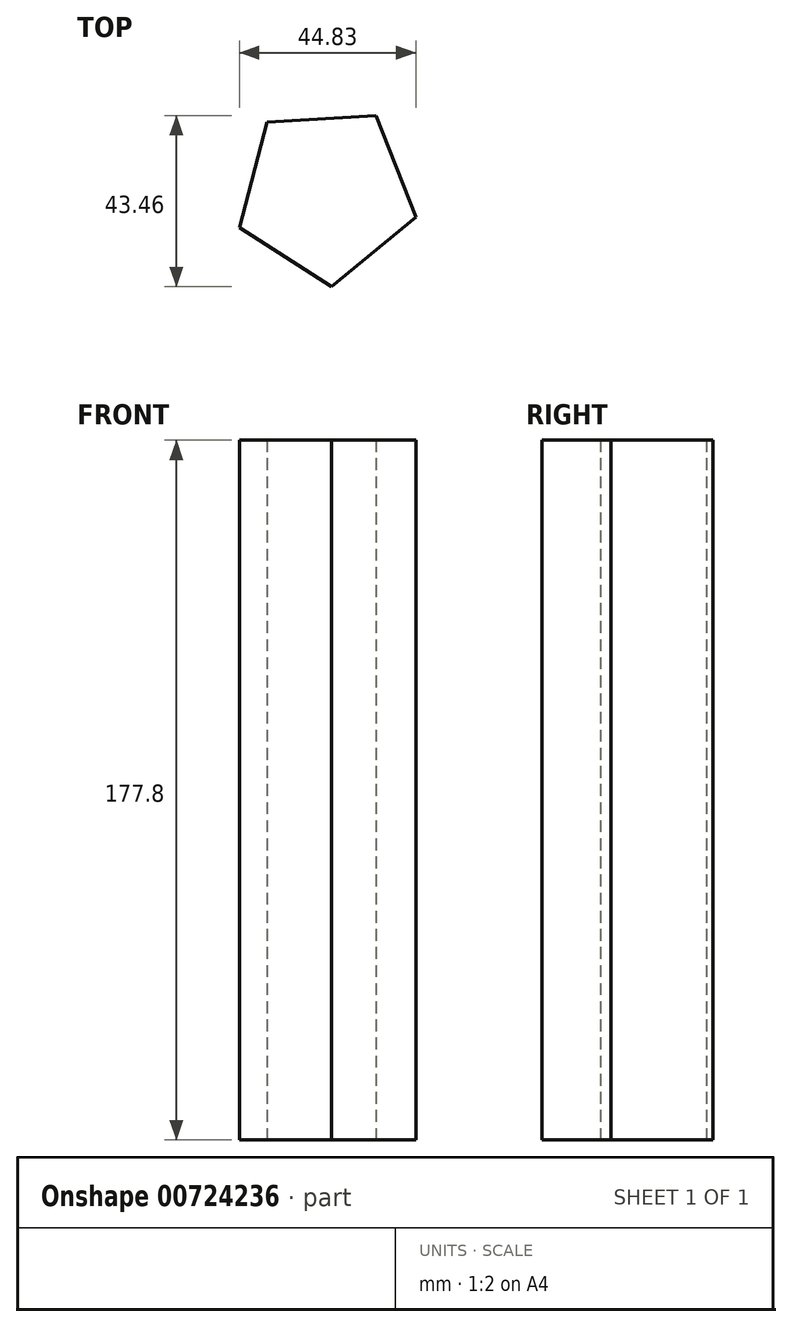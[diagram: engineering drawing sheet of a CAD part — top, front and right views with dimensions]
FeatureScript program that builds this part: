
annotation { "Feature Type Name" : "Feature", "Feature Type Description" : "" }
export const myFeature = defineFeature(function(context is Context, id is Id, definition is map)
    precondition{}
    {
        {
            var Q0;
            Q0=qCreatedBy(makeId("Top.planeOp"),FACE);
            var sketch = newSketch(context, id + "F0", { "sketchPlane" : qUnion([Q0])});
            skCircle(sketch, "E0.cCircle", {"center": v(-36.82, 14.76) * mm, "radius": 19.1 * mm, "construction": true});
            skLineSegment(sketch, "E0.0", {"start": v(-13.97, 8.8) * mm, "end": v(-35.42, -8.8) * mm});
            skLineSegment(sketch, "E0.1", {"start": v(-35.42, -8.8) * mm, "end": v(-58.8, 6.15) * mm});
            skLineSegment(sketch, "E0.2", {"start": v(-58.8, 6.15) * mm, "end": v(-51.8, 33.01) * mm});
            skLineSegment(sketch, "E0.3", {"start": v(-51.8, 33.01) * mm, "end": v(-24.1, 34.65) * mm});
            skLineSegment(sketch, "E0.4", {"start": v(-24.1, 34.65) * mm, "end": v(-13.97, 8.8) * mm});
            skPoint(sketch, "E0.0.midPoint", {"position": v(-24.7, 0) * mm});
            skSolve(sketch);
        }
        {
            var Q0;
            Q0=makeQuery(id+"F0.imprint","IMPRINT",FACE,{"disambiguationData":[TD([[makeQuery(id+"F0.imprint","IMPRINT",EDGE,{"derivedFrom":sQuery(id+"F0.wireOp",EDGE,"E0.0")}),-1.0]])]});
            extrude(context, id + "F1", {"entities" : qUnion([Q0]), "depth" : 177.8 * mm, "offsetDistance" : 25.4 * mm});
        }
        {
            var Q0;
            Q0=makeQuery(id+"F1.opExtrude","CAP_FACE",FACE,{"disambiguationData":[OSD([sQuery(id+"F0.wireOp",EDGE,"E0.0"),sQuery(id+"F0.wireOp",EDGE,"E0.1"),sQuery(id+"F0.wireOp",EDGE,"E0.2"),sQuery(id+"F0.wireOp",EDGE,"E0.3"),sQuery(id+"F0.wireOp",EDGE,"E0.4")])],"isStart":false});
            shell(context, id + "F2", {"entities" : qUnion([Q0]), "thickness" : 3 / 228.6 * mm});
        }
    });
